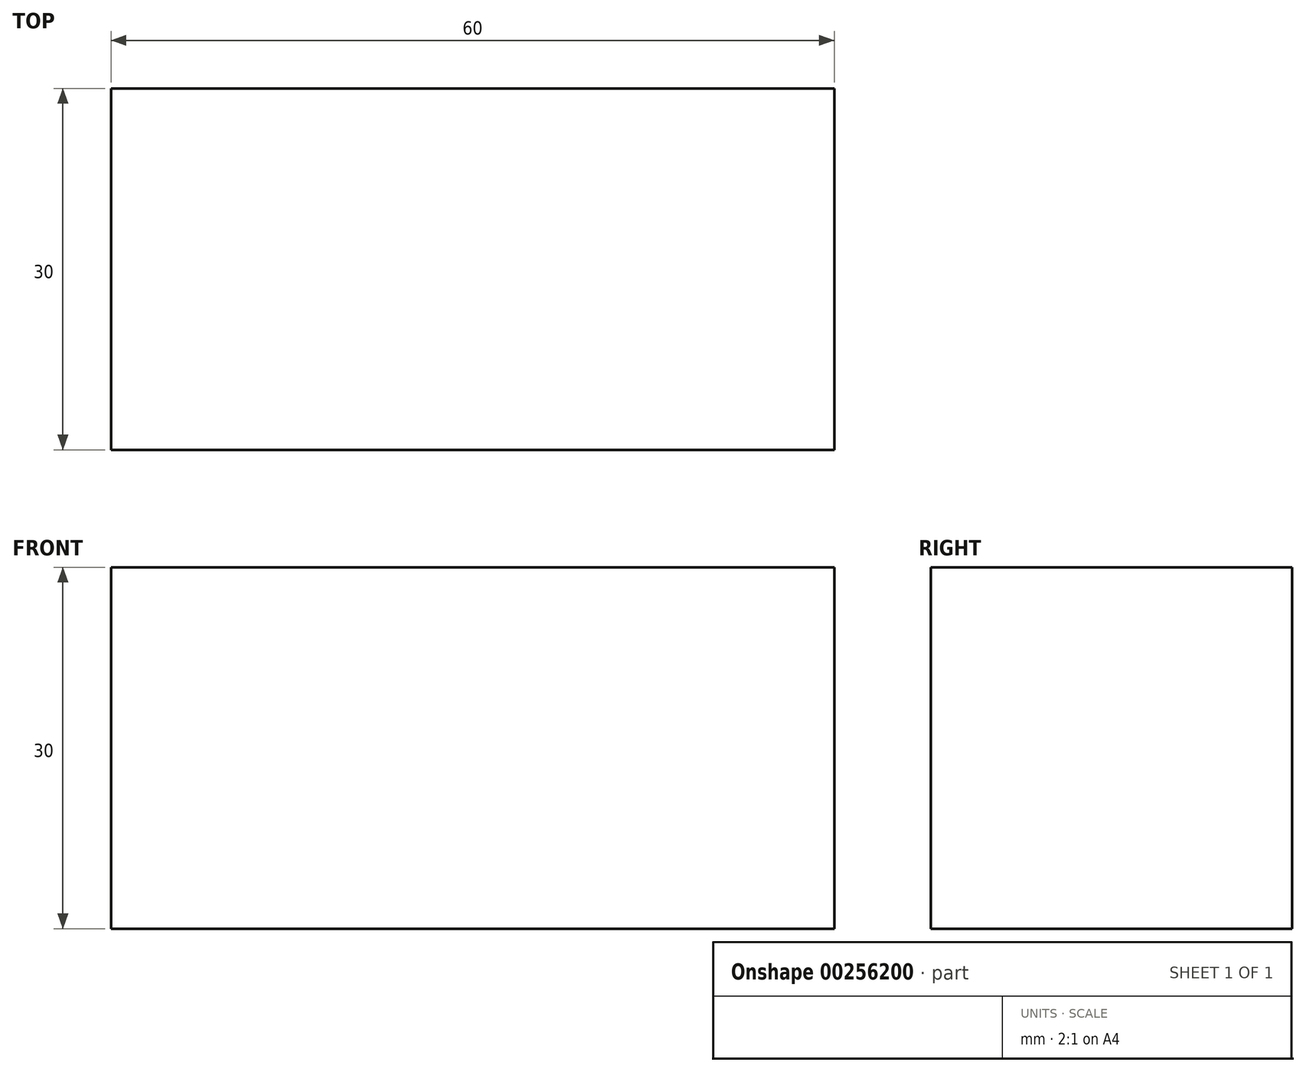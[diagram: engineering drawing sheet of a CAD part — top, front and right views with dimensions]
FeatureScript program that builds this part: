
annotation { "Feature Type Name" : "Feature", "Feature Type Description" : "" }
export const myFeature = defineFeature(function(context is Context, id is Id, definition is map)
    precondition{}
    {
        {
            var Q0;
            Q0=qCreatedBy(makeId("Front.planeOp"),FACE);
            var sketch = newSketch(context, id + "F0", { "sketchPlane" : qUnion([Q0])});
            skLineSegment(sketch, "E0.bottom", {"start": v(0, 0) * mm, "end": v(60, 0) * mm});
            skLineSegment(sketch, "E0.top", {"start": v(0, -30) * mm, "end": v(60, -30) * mm});
            skLineSegment(sketch, "E0.left", {"start": v(0, 0) * mm, "end": v(0, -30) * mm});
            skLineSegment(sketch, "E0.right", {"start": v(60, 0) * mm, "end": v(60, -30) * mm});
            skSolve(sketch);
        }
        {
            var Q0;
            Q0 = qSketchRegion(id + "F0", true);
            extrude(context, id + "F1", {"entities" : qUnion([Q0]), "depth" : 30 * mm});
        }
    });
